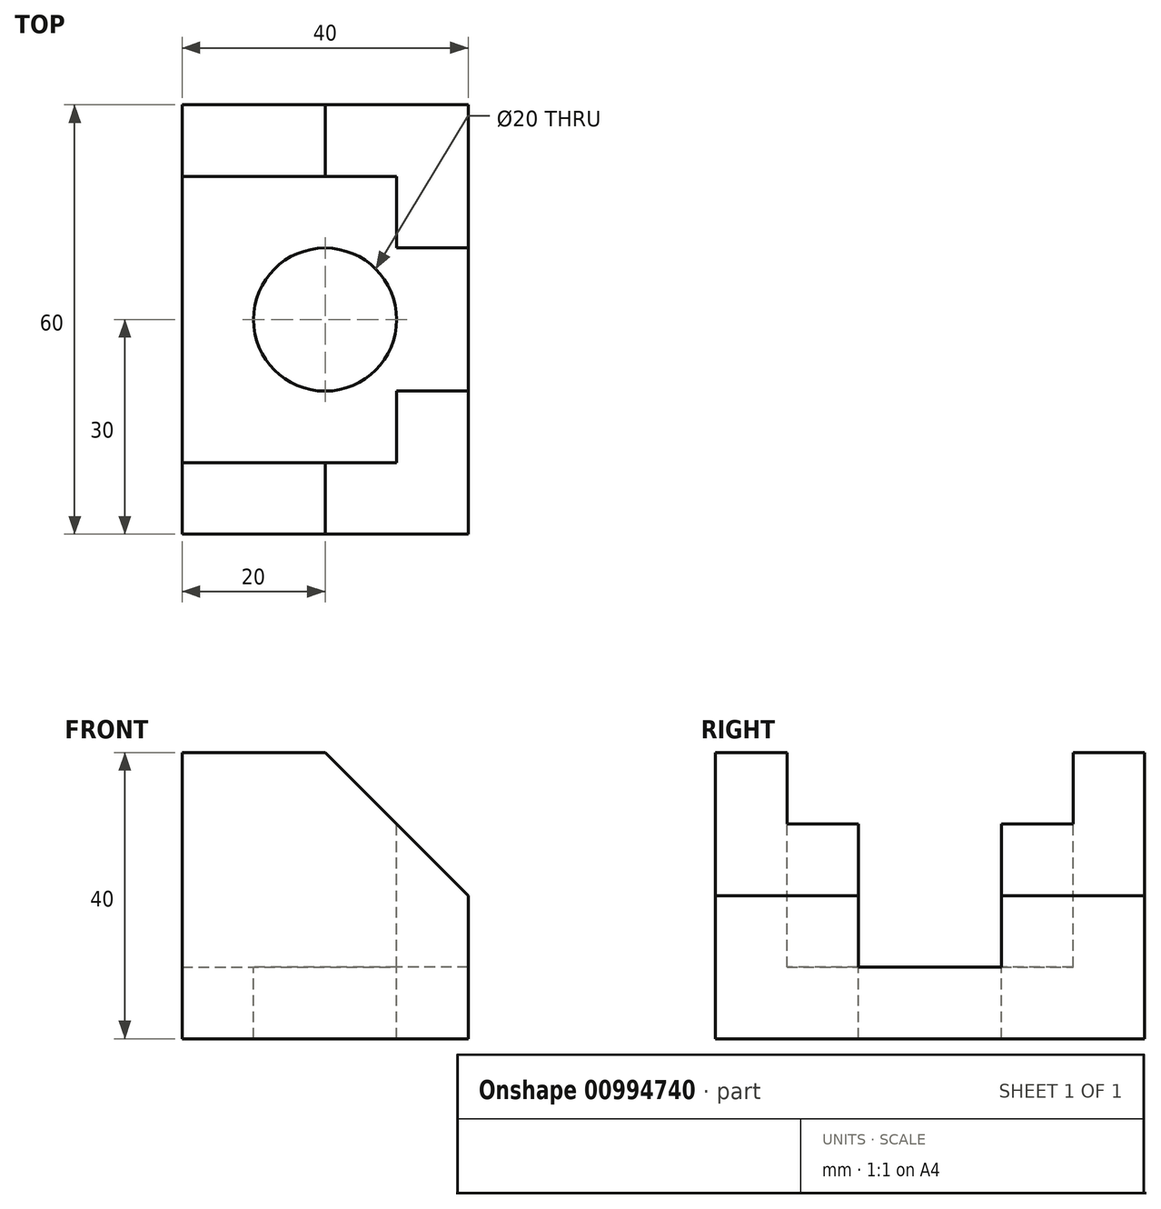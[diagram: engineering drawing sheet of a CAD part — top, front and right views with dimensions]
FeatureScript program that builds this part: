
annotation { "Feature Type Name" : "Feature", "Feature Type Description" : "" }
export const myFeature = defineFeature(function(context is Context, id is Id, definition is map)
    precondition{}
    {
        {
            var Q0;
            Q0=qCreatedBy(makeId("Front.planeOp"),FACE);
            var sketch = newSketch(context, id + "F0", { "sketchPlane" : qUnion([Q0])});
            skLineSegment(sketch, "E0.bottom", {"start": v(-20, 40) * mm, "end": v(0, 40) * mm});
            skLineSegment(sketch, "E0.top", {"start": v(-20, 0) * mm, "end": v(20, 0) * mm});
            skLineSegment(sketch, "E0.left", {"start": v(-20, 40) * mm, "end": v(-20, 0) * mm});
            skLineSegment(sketch, "E0.right", {"start": v(20, 20) * mm, "end": v(20, 0) * mm});
            skLineSegment(sketch, "E1", {"start": v(0, 40) * mm, "end": v(20, 20) * mm});
            skSolve(sketch);
        }
        {
            var Q0;
            Q0=makeQuery(id+"F0.imprint","IMPRINT",FACE,{"disambiguationData":[TD([[makeQuery(id+"F0.imprint","IMPRINT",EDGE,{"derivedFrom":sQuery(id+"F0.wireOp",EDGE,"E0.bottom")}),-1.0]])]});
            extrude(context, id + "F1", {"entities" : qUnion([Q0]), "endBound" : BoundingType.SYMMETRIC, "depth" : 60 * mm, "offsetDistance" : 25 * mm});
        }
        {
            var Q0;
            Q0=makeQuery(id+"F1.opExtrude","SWEPT_FACE",FACE,{"disambiguationData":[OSD([sQuery(id+"F0.wireOp",EDGE,"E0.bottom")])]});
            var sketch = newSketch(context, id + "F2", { "sketchPlane" : qUnion([Q0])});
            skLineSegment(sketch, "E2", {"start": v(-20, 20) * mm, "end": v(10, 20) * mm});
            skLineSegment(sketch, "E3", {"start": v(10, 20) * mm, "end": v(10, 10) * mm});
            skLineSegment(sketch, "E4", {"start": v(10, 10) * mm, "end": v(20, 10) * mm});
            skLineSegment(sketch, "E5", {"start": v(20, 10) * mm, "end": v(20, -10) * mm});
            skLineSegment(sketch, "E6", {"start": v(20, -10) * mm, "end": v(10, -10) * mm});
            skLineSegment(sketch, "E7", {"start": v(10, -10) * mm, "end": v(10, -20) * mm});
            skLineSegment(sketch, "E8", {"start": v(10, -20) * mm, "end": v(-20, -20) * mm});
            skLineSegment(sketch, "E9", {"start": v(-20, -20) * mm, "end": v(-20, 20) * mm});
            skSolve(sketch);
        }
        {
            var Q0;
            {var subQ0=sQuery(id+"F2.wireOp",EDGE,"E9");Q0=makeQuery(id+"F2.imprint","IMPRINT",FACE,{"disambiguationData":[TD([[makeQuery(id+"F2.imprint","IMPRINT",EDGE,{"derivedFrom":subQ0}),-1.0]])]});}
            var Q1;
            {var subQ0=sQuery(id+"F2.wireOp",EDGE,"E3");Q1=makeQuery(id+"F2.imprint","IMPRINT",FACE,{"disambiguationData":[TD([[makeQuery(id+"F2.imprint","IMPRINT",EDGE,{"derivedFrom":subQ0}),-1.0]])]});}
            extrude(context, id + "F3", {"entities" : qUnion([Q0, Q1]), "operationType" : NewBodyOperationType.REMOVE, "oppositeDirection" : true, "depth" : 30 * mm, "offsetDistance" : 25 * mm});
        }
        {
            var Q0;
            Q0=makeQuery(id+"F3.boolean.opBoolean","COPY",FACE,{"derivedFrom":makeQuery(id+"F3.opExtrude","CAP_FACE",FACE,{"disambiguationData":[OSD([sQuery(id+"F2.wireOp",EDGE,"E2"),sQuery(id+"F2.wireOp",EDGE,"E3"),sQuery(id+"F2.wireOp",EDGE,"E4"),sQuery(id+"F2.wireOp",EDGE,"E5"),sQuery(id+"F2.wireOp",EDGE,"E6"),sQuery(id+"F2.wireOp",EDGE,"E7"),sQuery(id+"F2.wireOp",EDGE,"E8"),sQuery(id+"F2.wireOp",EDGE,"E9")])],"isStart":false})});
            var sketch = newSketch(context, id + "F4", { "sketchPlane" : qUnion([Q0])});
            skCircle(sketch, "E10", {"center": v(0, 0) * mm, "radius": 10 * mm});
            skSolve(sketch);
        }
        {
            var Q0;
            Q0=makeQuery(id+"F4.imprint","IMPRINT",FACE,{"disambiguationData":[TD([[makeQuery(id+"F4.imprint","IMPRINT",EDGE,{"derivedFrom":sQuery(id+"F4.wireOp",EDGE,"E10")}),1.0]])]});
            var Q1;
            Q1=makeQuery(id+"F1.opExtrude","SWEPT_FACE",FACE,{"disambiguationData":[OSD([sQuery(id+"F0.wireOp",EDGE,"E0.top")])]});
            extrude(context, id + "F5", {"entities" : qUnion([Q0]), "operationType" : NewBodyOperationType.REMOVE, "endBound" : BoundingType.UP_TO_SURFACE, "oppositeDirection" : true, "depth" : 25 * mm, "endBoundEntityFace" : qUnion([Q1]), "offsetDistance" : 25 * mm});
        }
    });
